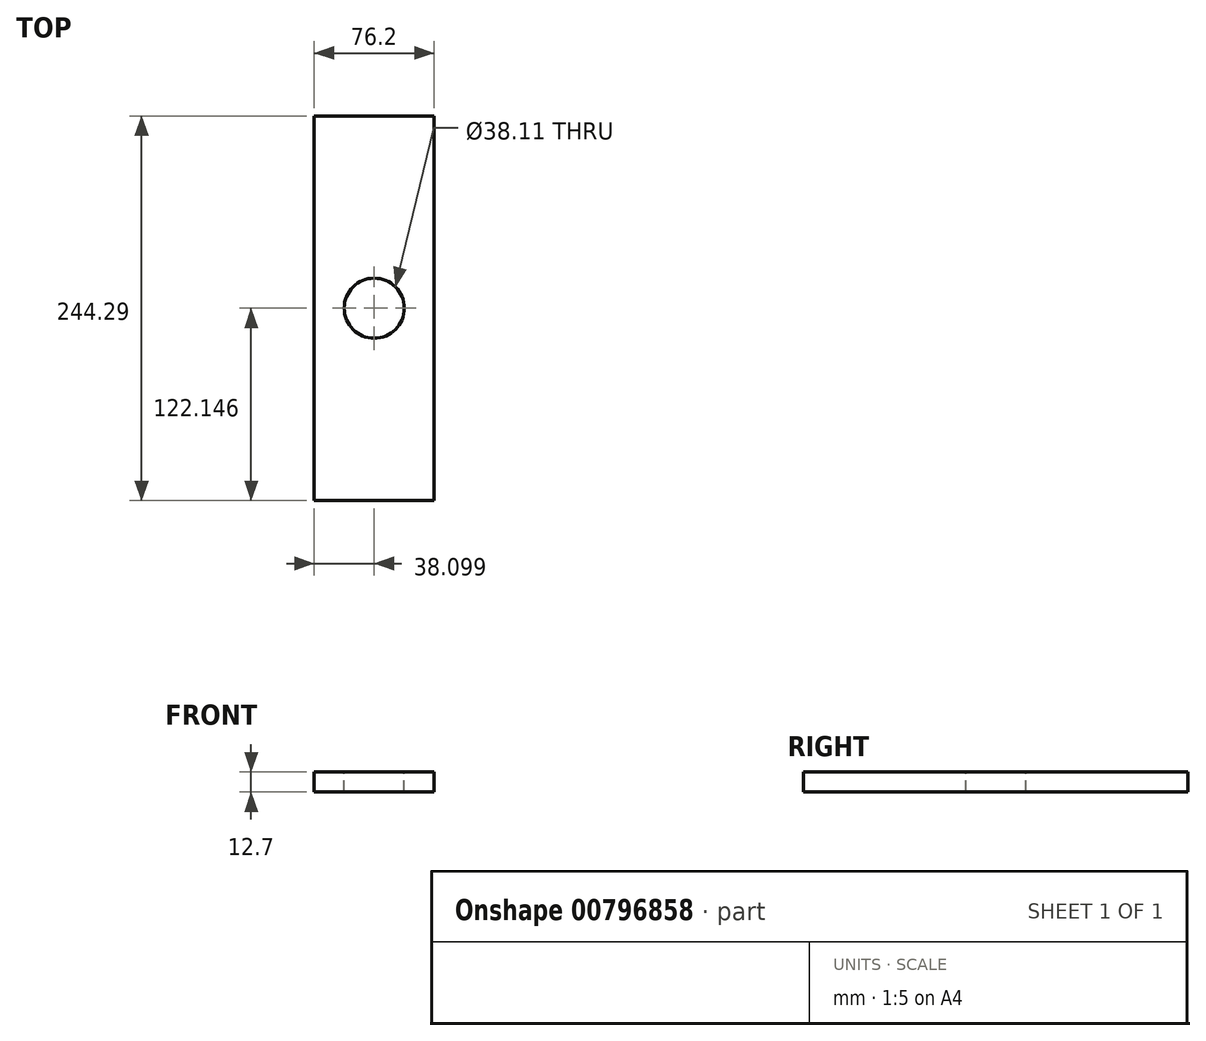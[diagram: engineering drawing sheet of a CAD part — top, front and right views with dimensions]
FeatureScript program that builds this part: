
annotation { "Feature Type Name" : "Feature", "Feature Type Description" : "" }
export const myFeature = defineFeature(function(context is Context, id is Id, definition is map)
    precondition{}
    {
        {
            var Q0;
            Q0=qCreatedBy(makeId("Top.planeOp"),FACE);
            var sketch = newSketch(context, id + "F0", { "sketchPlane" : qUnion([Q0])});
            skLineSegment(sketch, "E0.bottom", {"start": v(-37.21, 113.67) * mm, "end": v(38.99, 113.67) * mm});
            skLineSegment(sketch, "E0.top", {"start": v(-37.21, -130.62) * mm, "end": v(38.99, -130.62) * mm});
            skLineSegment(sketch, "E0.left", {"start": v(-37.21, 113.67) * mm, "end": v(-37.21, -130.62) * mm});
            skLineSegment(sketch, "E0.right", {"start": v(38.99, 113.67) * mm, "end": v(38.99, -130.62) * mm});
            skPoint(sketch, "E0.middle", {"position": v(0.89, -8.47) * mm});
            skCircle(sketch, "E1", {"center": v(0.89, -8.47) * mm, "radius": 19.05 * mm});
            skSolve(sketch);
        }
        {
            var Q0;
            Q0=makeQuery(id+"F0.imprint","IMPRINT",FACE,{"disambiguationData":[TD([[makeQuery(id+"F0.imprint","IMPRINT",EDGE,{"derivedFrom":sQuery(id+"F0.wireOp",EDGE,"E0.bottom")}),-1.0]])]});
            extrude(context, id + "F1", {"entities" : qUnion([Q0]), "oppositeDirection" : true, "depth" : 12.7 * mm, "offsetDistance" : 25.4 * mm});
        }
    });
